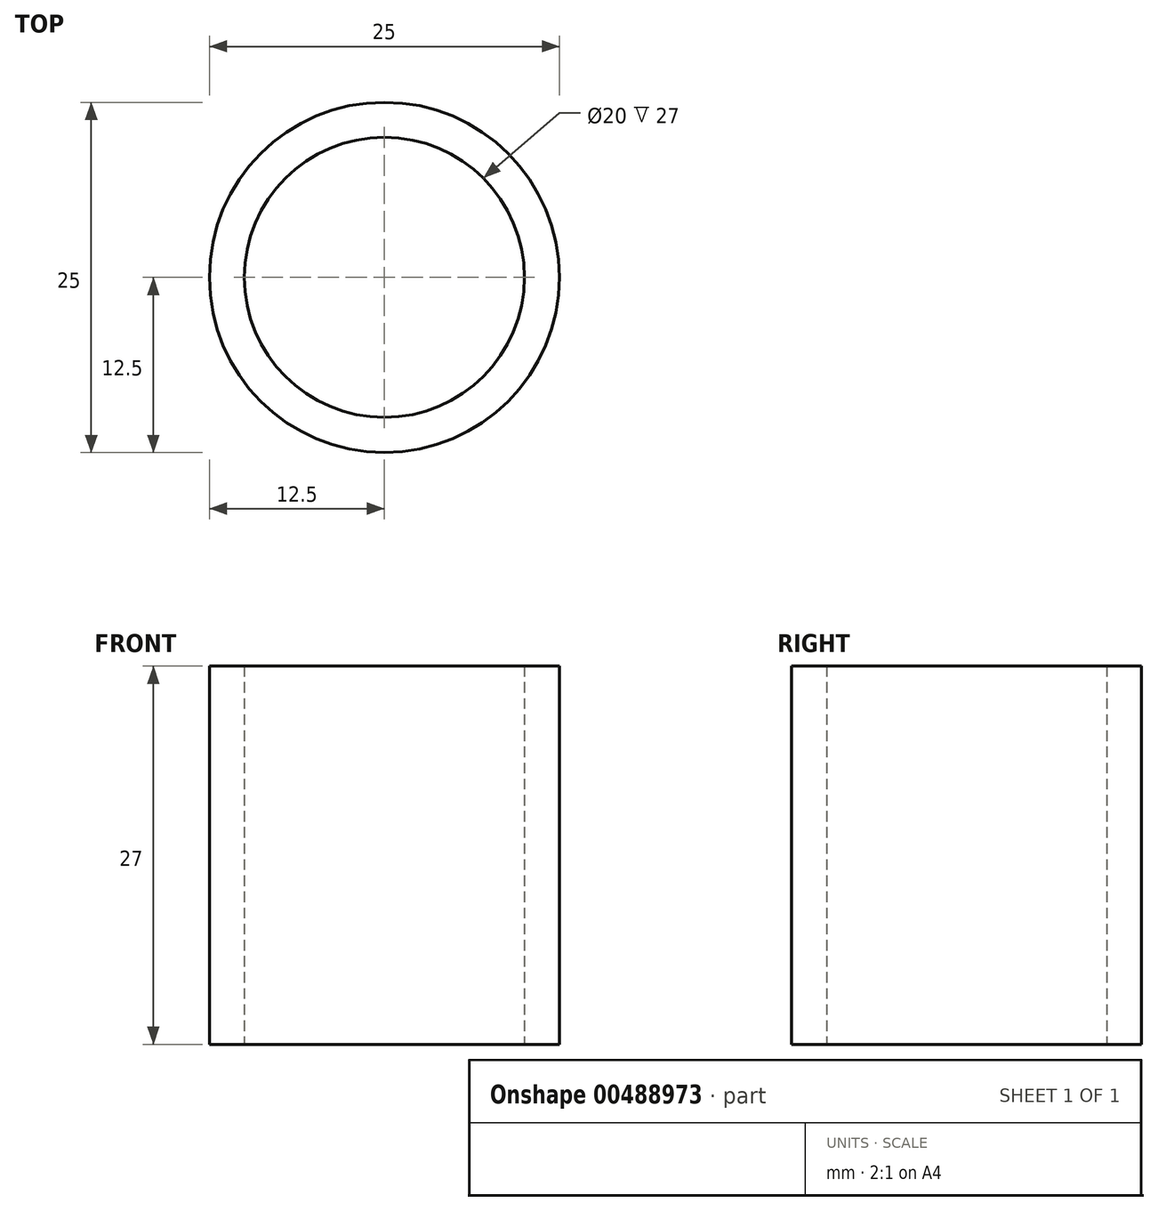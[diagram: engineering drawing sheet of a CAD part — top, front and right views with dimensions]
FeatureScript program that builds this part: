
annotation { "Feature Type Name" : "Feature", "Feature Type Description" : "" }
export const myFeature = defineFeature(function(context is Context, id is Id, definition is map)
    precondition{}
    {
        {
            var Q0;
            Q0=qCreatedBy(makeId("Top.planeOp"),FACE);
            var sketch = newSketch(context, id + "F0", { "sketchPlane" : qUnion([Q0])});
            skCircle(sketch, "E0", {"center": v(0, 0) * mm, "radius": 12.5 * mm});
            skCircle(sketch, "E1", {"center": v(0, 0) * mm, "radius": 10 * mm});
            skSolve(sketch);
        }
        {
            var Q0;
            Q0=makeQuery(id+"F0.imprint","IMPRINT",FACE,{"disambiguationData":[TD([[makeQuery(id+"F0.imprint","IMPRINT",EDGE,{"derivedFrom":sQuery(id+"F0.wireOp",EDGE,"E0")}),1.0]])]});
            extrude(context, id + "F1", {"entities" : qUnion([Q0]), "depth" : 27 * mm});
        }
    });
